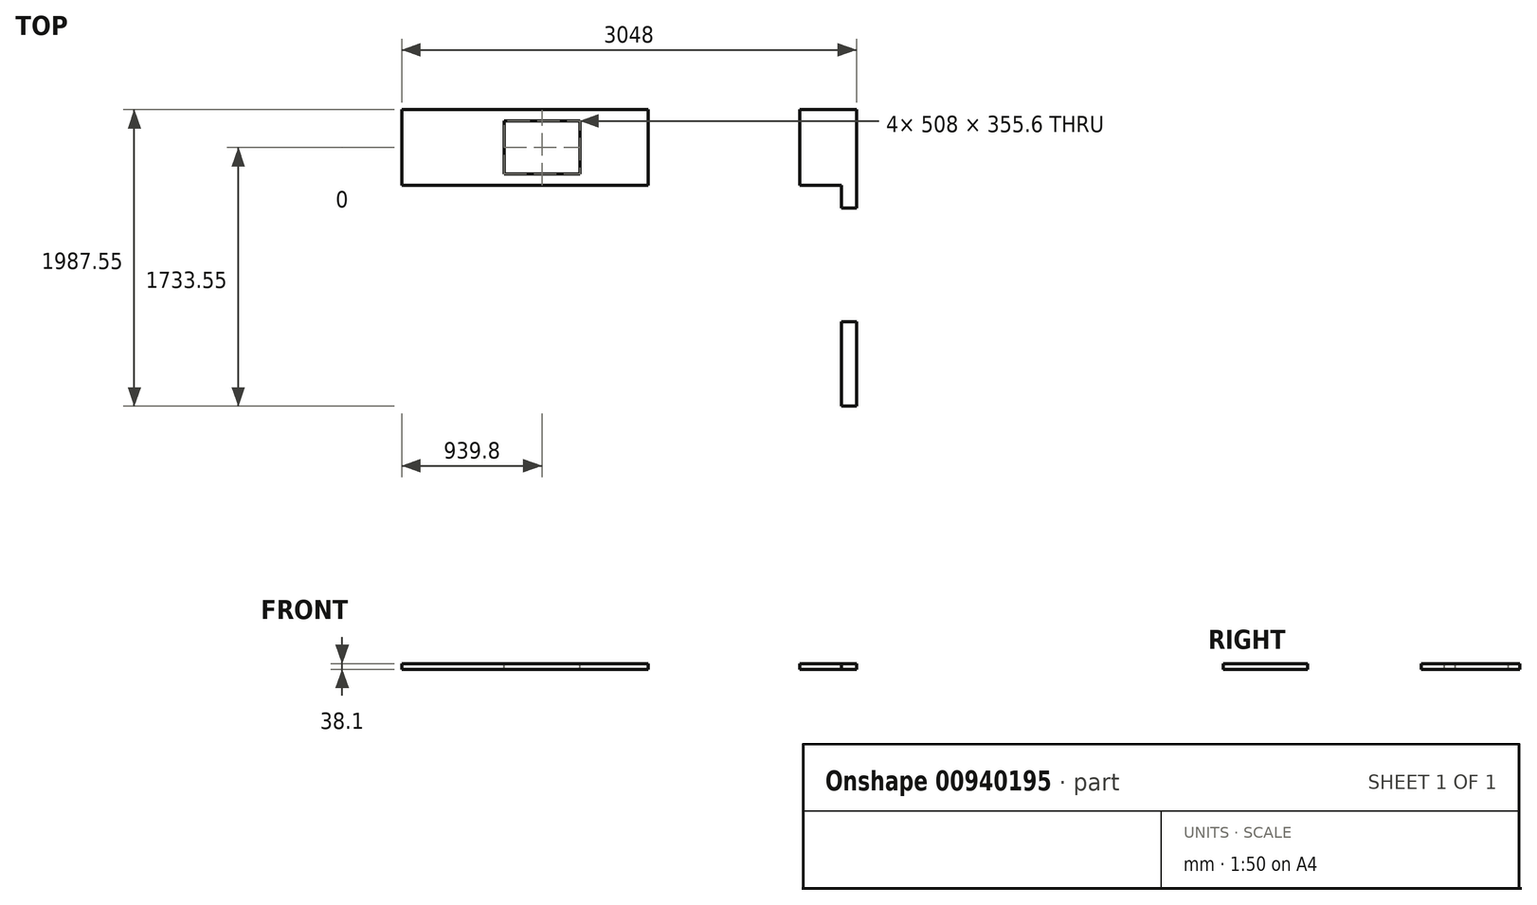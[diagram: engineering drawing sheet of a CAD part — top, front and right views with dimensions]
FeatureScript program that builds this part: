
annotation { "Feature Type Name" : "Feature", "Feature Type Description" : "" }
export const myFeature = defineFeature(function(context is Context, id is Id, definition is map)
    precondition{}
    {
        {
            var Q0;
            Q0=qCreatedBy(makeId("Top.planeOp"),FACE);
            var sketch = newSketch(context, id + "F0", { "sketchPlane" : qUnion([Q0])});
            skLineSegment(sketch, "E0.bottom", {"start": v(825.5, -254) * mm, "end": v(-825.5, -254) * mm});
            skLineSegment(sketch, "E0.top", {"start": v(825.5, 254) * mm, "end": v(-825.5, 254) * mm});
            skLineSegment(sketch, "E0.left", {"start": v(825.5, -254) * mm, "end": v(825.5, 254) * mm});
            skLineSegment(sketch, "E0.right", {"start": v(-825.5, -254) * mm, "end": v(-825.5, 254) * mm});
            skPoint(sketch, "E0.middle", {"position": v(0, 0) * mm});
            skLineSegment(sketch, "E1", {"start": v(1841.5, 254) * mm, "end": v(2222.5, 254) * mm});
            skLineSegment(sketch, "E2", {"start": v(2222.5, 254) * mm, "end": v(2222.5, -406.4) * mm});
            skLineSegment(sketch, "E3", {"start": v(2222.5, -406.4) * mm, "end": v(2120.9, -406.4) * mm});
            skLineSegment(sketch, "E4", {"start": v(2120.9, -406.4) * mm, "end": v(2120.9, -254) * mm});
            skLineSegment(sketch, "E5", {"start": v(2120.9, -254) * mm, "end": v(1841.5, -254) * mm});
            skLineSegment(sketch, "E6", {"start": v(1841.5, -254) * mm, "end": v(1841.5, 254) * mm});
            skLineSegment(sketch, "E7.bottom", {"start": v(2222.5, -1168.4) * mm, "end": v(2120.9, -1168.4) * mm});
            skLineSegment(sketch, "E7.top", {"start": v(2222.5, -1733.55) * mm, "end": v(2120.9, -1733.55) * mm});
            skLineSegment(sketch, "E7.left", {"start": v(2222.5, -1168.4) * mm, "end": v(2222.5, -1733.55) * mm});
            skLineSegment(sketch, "E7.right", {"start": v(2120.9, -1168.4) * mm, "end": v(2120.9, -1733.55) * mm});
            skSolve(sketch);
        }
        {
            var Q0;
            Q0=makeQuery(id+"F0.imprint","IMPRINT",FACE,{"disambiguationData":[TD([[makeQuery(id+"F0.imprint","IMPRINT",EDGE,{"derivedFrom":sQuery(id+"F0.wireOp",EDGE,"E0.bottom")}),-1.0]])]});
            var Q1;
            Q1=makeQuery(id+"F0.imprint","IMPRINT",FACE,{"disambiguationData":[TD([[makeQuery(id+"F0.imprint","IMPRINT",EDGE,{"derivedFrom":sQuery(id+"F0.wireOp",EDGE,"E1")}),-1.0]])]});
            var Q2;
            Q2=makeQuery(id+"F0.imprint","IMPRINT",FACE,{"disambiguationData":[TD([[makeQuery(id+"F0.imprint","IMPRINT",EDGE,{"derivedFrom":sQuery(id+"F0.wireOp",EDGE,"E7.bottom")}),1.0]])]});
            extrude(context, id + "F1", {"entities" : qUnion([Q0, Q1, Q2]), "depth" : 38.1 * mm, "offsetDistance" : 25.4 * mm});
        }
        {
            var Q0;
            Q0=makeQuery(id+"F1.opExtrude","CAP_FACE",FACE,{"disambiguationData":[OSD([sQuery(id+"F0.wireOp",EDGE,"E0.bottom"),sQuery(id+"F0.wireOp",EDGE,"E0.top"),sQuery(id+"F0.wireOp",EDGE,"E0.left"),sQuery(id+"F0.wireOp",EDGE,"E0.right")])],"isStart":false});
            var sketch = newSketch(context, id + "F2", { "sketchPlane" : qUnion([Q0])});
            skLineSegment(sketch, "E8.bottom", {"start": v(368.3, -177.8) * mm, "end": v(-139.7, -177.8) * mm});
            skLineSegment(sketch, "E8.top", {"start": v(368.3, 177.8) * mm, "end": v(-139.7, 177.8) * mm});
            skLineSegment(sketch, "E8.left", {"start": v(368.3, -177.8) * mm, "end": v(368.3, 177.8) * mm});
            skLineSegment(sketch, "E8.right", {"start": v(-139.7, -177.8) * mm, "end": v(-139.7, 177.8) * mm});
            skPoint(sketch, "E8.middle", {"position": v(114.3, 0) * mm});
            skSolve(sketch);
        }
        {
            var Q0;
            Q0=makeQuery(id+"F2.imprint","IMPRINT",FACE,{"disambiguationData":[TD([[makeQuery(id+"F2.imprint","IMPRINT",EDGE,{"derivedFrom":sQuery(id+"F2.wireOp",EDGE,"E8.bottom")}),-1.0]])]});
            extrude(context, id + "F3", {"entities" : qUnion([Q0]), "operationType" : NewBodyOperationType.REMOVE, "oppositeDirection" : true, "depth" : 38.1 * mm, "offsetDistance" : 25.4 * mm});
        }
    });
